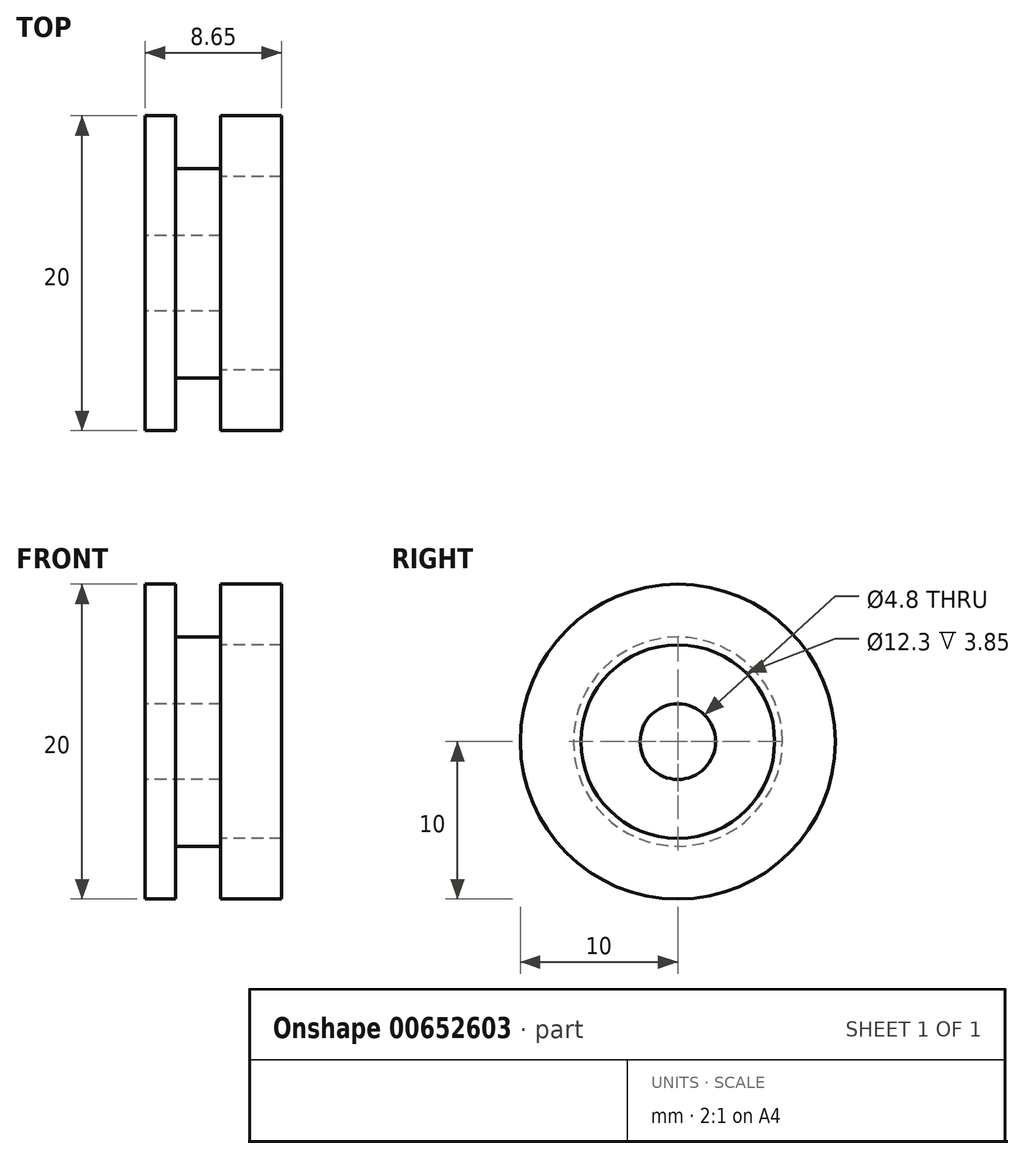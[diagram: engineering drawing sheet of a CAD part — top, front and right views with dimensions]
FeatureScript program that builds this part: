
annotation { "Feature Type Name" : "Feature", "Feature Type Description" : "" }
export const myFeature = defineFeature(function(context is Context, id is Id, definition is map)
    precondition{}
    {
        {
            var Q0;
            Q0=qCreatedBy(makeId("Front.planeOp"),FACE);
            var sketch = newSketch(context, id + "F0", { "sketchPlane" : qUnion([Q0])});
            skLineSegment(sketch, "E0", {"start": v(-5, 0) * mm, "end": v(-5, 10) * mm});
            skLineSegment(sketch, "E1", {"start": v(-5, 10) * mm, "end": v(-3.08, 10) * mm});
            skLineSegment(sketch, "E2", {"start": v(-3.08, 10) * mm, "end": v(-3.08, 6.64) * mm});
            skLineSegment(sketch, "E3", {"start": v(-3.08, 6.64) * mm, "end": v(-0.2, 6.64) * mm});
            skLineSegment(sketch, "E4", {"start": v(-0.2, 6.64) * mm, "end": v(-0.2, 10) * mm});
            skLineSegment(sketch, "E5", {"start": v(-0.2, 10) * mm, "end": v(3.65, 10) * mm});
            skPoint(sketch, "E6.end.orphan", {"position": v(-5, 2.4) * mm});
            skLineSegment(sketch, "E7", {"start": v(3.65, 10) * mm, "end": v(3.65, 6.15) * mm});
            skLineSegment(sketch, "E8", {"start": v(3.65, 6.15) * mm, "end": v(-0.2, 6.15) * mm});
            skLineSegment(sketch, "E9", {"start": v(-0.2, 6.15) * mm, "end": v(-0.2, 2.4) * mm});
            skLineSegment(sketch, "E10", {"start": v(-0.2, 2.4) * mm, "end": v(-5, 2.4) * mm});
            skLineSegment(sketch, "E11", {"start": v(-5, 0) * mm, "end": v(34.3, 0) * mm, "construction": true});
            skSolve(sketch);
        }
        {
            var Q0;
            Q0 = qSketchRegion(id + "F0", true);
            var Q1;
            Q1=sQuery(id+"F0.wireOp",EDGE,"E11");
            revolve(context, id + "F1", {"entities" : qUnion([Q0]), "axis" : qUnion([Q1]), "revolveType" : RevolveType.FULL});
        }
    });
